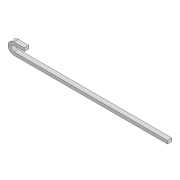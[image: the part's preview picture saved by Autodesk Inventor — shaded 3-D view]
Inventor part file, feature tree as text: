
AUTODESK INVENTOR PART (.ipt)
format: ipt  version: 2020.2 (Build 242310000, 310)  size: 84,480 bytes
history: native  units: mm
features: extrude x1, sketch x1
ambient origin geometry x8: Origin, YZ Plane, XZ Plane, XY Plane, X Axis, Y Axis, Z Axis, Center Point
bodies: Solid1 (feature_tree)
feature tree (2):
  extrude  "Extrusion1"  Depth=20.0mm
  sketch  "Sketch1"  dims[d0=76.0mm d1=20.0mm d2=20.0mm d4=1000.0mm d5=29.0mm d6=0.0mm d7=68.0mm]
